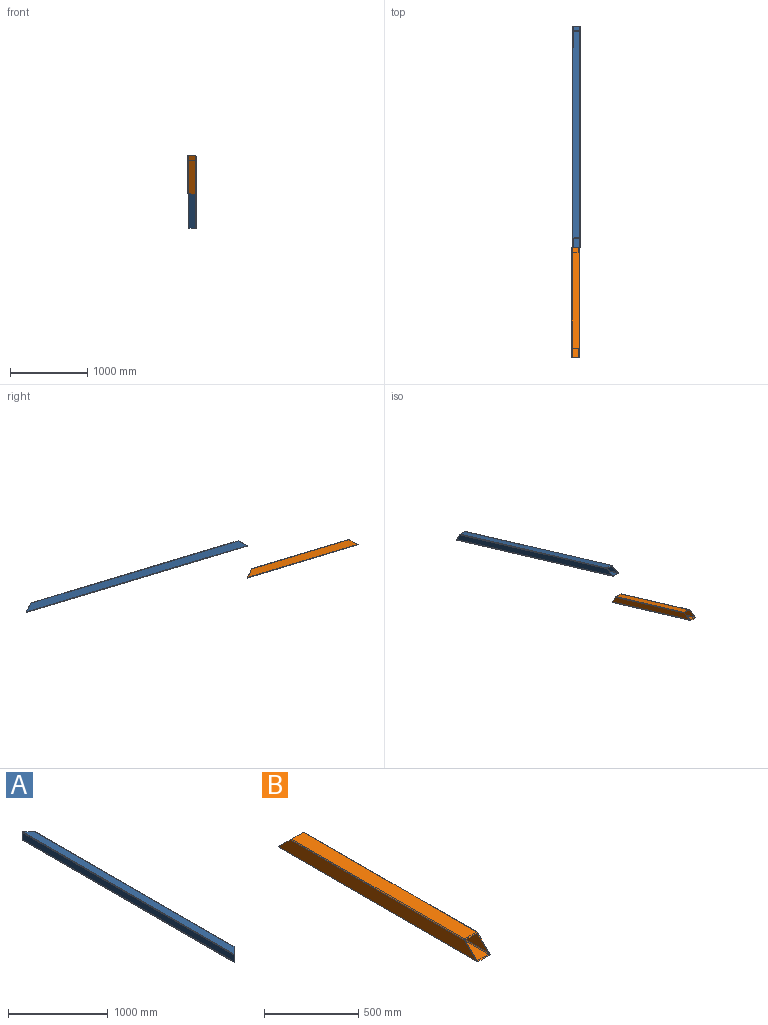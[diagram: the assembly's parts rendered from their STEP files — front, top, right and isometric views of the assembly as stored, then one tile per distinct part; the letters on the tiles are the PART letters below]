
ASSEMBLY  parts=2 mates=1
PART A: 18 faces, bbox 100x3000x100 mm
  f0: plane 2990x90mm, normal (0,0,1), area 261000mm2, adj f1,f15,f16,f17
  f1: cylinder r=5mm len=3000mm, axis (0,1,0), area 23533.4mm2, adj f0,f2,f16,f17
  f2: plane 3000x90mm, normal (-1,0,0), area 270000mm2, adj f1,f3,f16,f17
  f3: cylinder r=5mm len=3000mm, axis (0,1,0), area 23533.4mm2, adj f2,f4,f16,f17
  f4: plane 2990x90mm, normal (0,0,-1), area 261000mm2, adj f3,f5,f16,f17
  f5: cylinder r=5mm len=2810mm, axis (0,1,0), area 22019.7mm2, adj f4,f6,f16,f17
  f6: plane 2800x90mm, normal (1,0,0), area 252000mm2, adj f5,f15,f16,f17
  f7: cylinder r=5mm len=2990mm, axis (0,1,0), area 23454.9mm2, adj f8,f14,f16,f17
  f8: plane 2990x80mm, normal (1,0,0), area 239200mm2, adj f7,f9,f16,f17
  f9: cylinder r=5mm len=2990mm, axis (0,1,0), area 23454.9mm2, adj f8,f10,f16,f17
  f10: plane 2980x80mm, normal (0,0,-1), area 232000mm2, adj f9,f11,f16,f17
  f11: cylinder r=5mm len=2820mm, axis (0,1,0), area 22098.2mm2, adj f10,f12,f16,f17
  f12: plane 2810x80mm, normal (-1,0,0), area 224800mm2, adj f11,f13,f16,f17
  f13: cylinder r=5mm len=2820mm, axis (0,1,0), area 22098.2mm2, adj f12,f14,f16,f17
  f14: plane 2980x80mm, normal (0,0,1), area 232000mm2, adj f7,f13,f16,f17
  f15: cylinder r=5mm len=2810mm, axis (0,1,0), area 22019.7mm2, adj f0,f6,f16,f17
  f16: plane 100x100mm, normal (0.71,-0.71,0), area 2687mm2, adj f0,f1,f2,f3,f4,f5,f6,f7
  f17: plane 100x100mm, normal (0.71,0.71,0), area 2687mm2, adj f0,f1,f2,f3,f4,f5,f6,f7
PART B: 18 faces, bbox 100x1500x100 mm
  f0: plane 1300x90mm, normal (0,0,1), area 117000mm2, adj f1,f15,f16,f17
  f1: cylinder r=5mm len=1310mm, axis (0,1,0), area 10238.7mm2, adj f0,f2,f16,f17
  f2: plane 1490x90mm, normal (-1,0,0), area 126000mm2, adj f1,f3,f16,f17
  f3: cylinder r=5mm len=1500mm, axis (0,1,0), area 11752.4mm2, adj f2,f4,f16,f17
  f4: plane 1500x90mm, normal (0,0,-1), area 135000mm2, adj f3,f5,f16,f17
  f5: cylinder r=5mm len=1500mm, axis (0,1,0), area 11752.4mm2, adj f4,f6,f16,f17
  f6: plane 1490x90mm, normal (1,0,0), area 126000mm2, adj f5,f15,f16,f17
  f7: cylinder r=5mm len=1490mm, axis (0,1,0), area 11673.9mm2, adj f8,f14,f16,f17
  f8: plane 1480x80mm, normal (1,0,0), area 112000mm2, adj f7,f9,f16,f17
  f9: cylinder r=5mm len=1320mm, axis (0,1,0), area 10317.3mm2, adj f8,f10,f16,f17
  f10: plane 1310x80mm, normal (0,0,-1), area 104800mm2, adj f9,f11,f16,f17
  f11: cylinder r=5mm len=1320mm, axis (0,1,0), area 10317.3mm2, adj f10,f12,f16,f17
  f12: plane 1480x80mm, normal (-1,0,0), area 112000mm2, adj f11,f13,f16,f17
  f13: cylinder r=5mm len=1490mm, axis (0,1,0), area 11673.9mm2, adj f12,f14,f16,f17
  f14: plane 1490x80mm, normal (0,0,1), area 119200mm2, adj f7,f13,f16,f17
  f15: cylinder r=5mm len=1310mm, axis (0,1,0), area 10238.7mm2, adj f0,f6,f16,f17
  f16: plane 100x100mm, normal (0,0.71,0.71), area 2687mm2, adj f0,f1,f2,f3,f4,f5,f6,f7
  f17: plane 100x100mm, normal (0,-0.71,0.71), area 2687mm2, adj f0,f1,f2,f3,f4,f5,f6,f7
PLACE A rot(axis=(-0.15,-0.98,0.14),90deg) t=(895.59,-244.45,-234.73)mm
PLACE B rot(axis=(0.01,0.15,0.99),179.8deg) t=(887.09,-4548.66,642.45)mm
MATE planar B.f2 <-> A.f4  axis (1,-0.01,-0.02) through (937.06,-3830.86,425.03)mm
